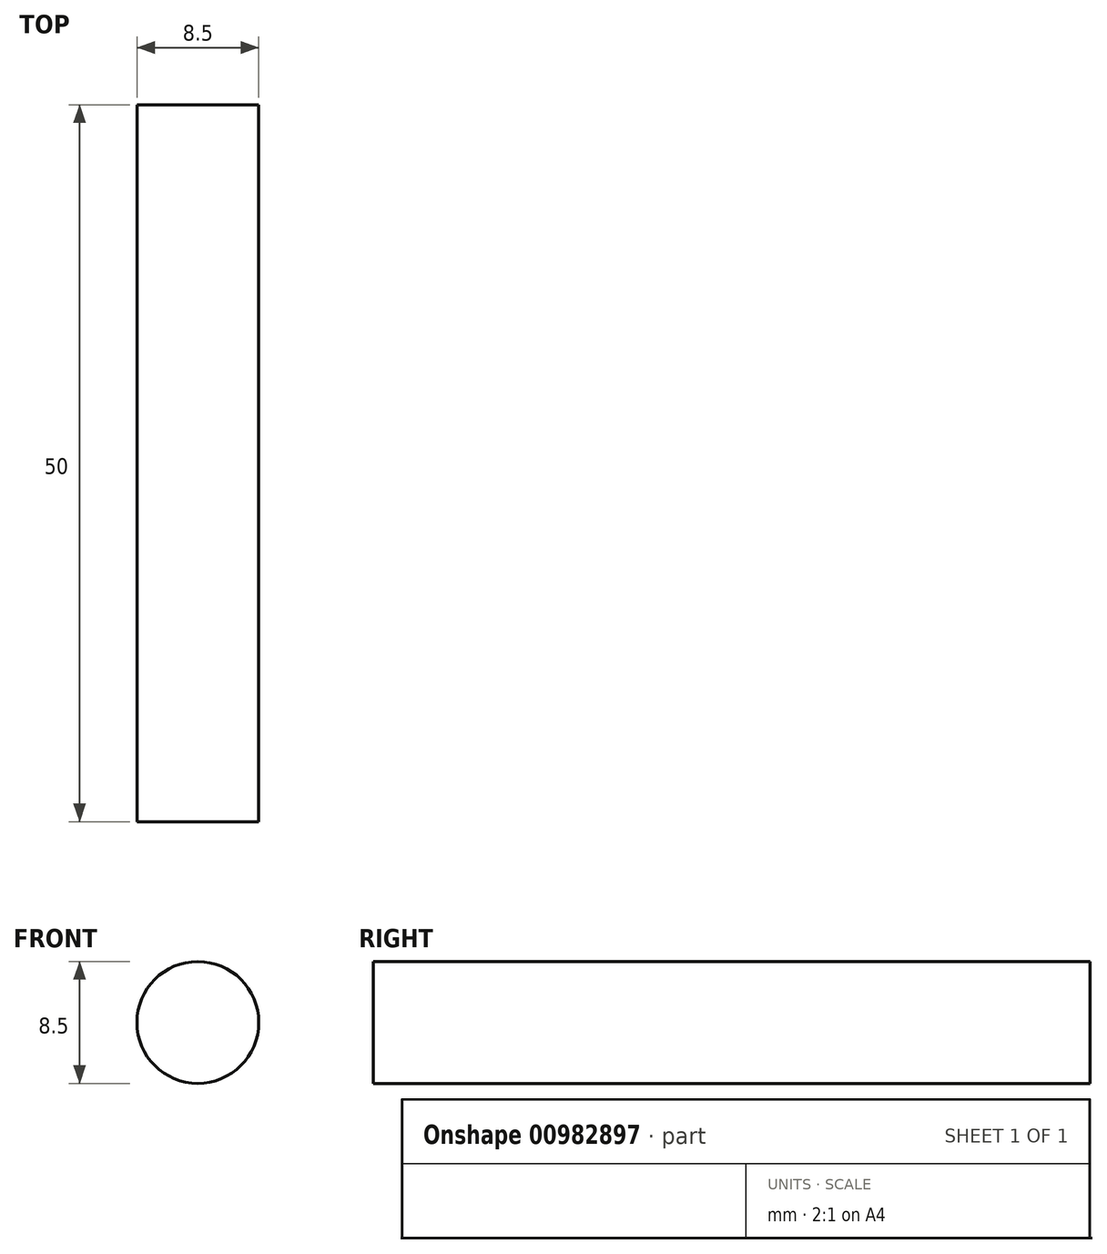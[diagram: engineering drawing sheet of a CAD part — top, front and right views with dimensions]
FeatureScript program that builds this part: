
annotation { "Feature Type Name" : "Feature", "Feature Type Description" : "" }
export const myFeature = defineFeature(function(context is Context, id is Id, definition is map)
    precondition{}
    {
        {
            var Q0;
            Q0=qCreatedBy(makeId("Top.planeOp"),FACE);
            var sketch = newSketch(context, id + "F0", { "sketchPlane" : qUnion([Q0])});
            skPoint(sketch, "E0", {"position": v(34.15, 0) * mm});
            skLineSegment(sketch, "E1", {"start": v(34.15, 25) * mm, "end": v(34.15, -25) * mm});
            skLineSegment(sketch, "E2", {"start": v(34.15, -25) * mm, "end": v(-34.15, -25) * mm});
            skLineSegment(sketch, "E3", {"start": v(-34.15, -25) * mm, "end": v(-34.15, 25) * mm});
            skLineSegment(sketch, "E4", {"start": v(-34.15, 25) * mm, "end": v(34.15, 25) * mm});
            skCircle(sketch, "E5", {"center": v(0, 0) * mm, "radius": 11 * mm});
            skLineSegment(sketch, "E6.bottom", {"start": v(15.5, -15.5) * mm, "end": v(-15.5, -15.5) * mm, "construction": true});
            skLineSegment(sketch, "E6.top", {"start": v(15.5, 15.5) * mm, "end": v(-15.5, 15.5) * mm, "construction": true});
            skLineSegment(sketch, "E6.left", {"start": v(15.5, -15.5) * mm, "end": v(15.5, 15.5) * mm, "construction": true});
            skLineSegment(sketch, "E6.right", {"start": v(-15.5, -15.5) * mm, "end": v(-15.5, 15.5) * mm, "construction": true});
            skCircle(sketch, "E7", {"center": v(-15.5, 15.5) * mm, "radius": 2 * mm});
            skCircle(sketch, "E8.1.0", {"center": v(-15.5, -15.5) * mm, "radius": 2 * mm});
            skCircle(sketch, "E8.2.0", {"center": v(15.5, -15.5) * mm, "radius": 2 * mm});
            skCircle(sketch, "E8.3.0", {"center": v(15.5, 15.5) * mm, "radius": 2 * mm});
            skSolve(sketch);
        }
        {
            var Q0;
            Q0=makeQuery(id+"F0.imprint","IMPRINT",FACE,{"disambiguationData":[TD([[makeQuery(id+"F0.imprint","IMPRINT",EDGE,{"derivedFrom":sQuery(id+"F0.wireOp",EDGE,"E1")}),-1.0]])]});
            extrude(context, id + "F1", {"entities" : qUnion([Q0]), "depth" : 15 * mm, "offsetDistance" : 25 * mm});
        }
        {
            var Q0;
            Q0=makeQuery(id+"F1.opExtrude","SWEPT_FACE",FACE,{"disambiguationData":[OSD([sQuery(id+"F0.wireOp",EDGE,"E2")])]});
            var sketch = newSketch(context, id + "F2", { "sketchPlane" : qUnion([Q0])});
            skCircle(sketch, "E9", {"center": v(-26.15, 7.5) * mm, "radius": 4.25 * mm});
            skPoint(sketch, "E9.centerSnap0", {"position": v(-34.15, 7.5) * mm});
            skCircle(sketch, "E10.MirrorC", {"center": v(26.15, 7.5) * mm, "radius": 4.25 * mm});
            skSolve(sketch);
        }
        {
            var Q0;
            Q0=makeQuery(id+"F2.imprint","IMPRINT",FACE,{"disambiguationData":[TD([[makeQuery(id+"F2.imprint","IMPRINT",EDGE,{"derivedFrom":sQuery(id+"F2.wireOp",EDGE,"E9")}),1.0]])]});
            var Q1;
            Q1=makeQuery(id+"F2.imprint","IMPRINT",FACE,{"disambiguationData":[TD([[makeQuery(id+"F2.imprint","IMPRINT",EDGE,{"derivedFrom":sQuery(id+"F2.wireOp",EDGE,"E10.MirrorC")}),-1.0]])]});
            extrude(context, id + "F3", {"entities" : qUnion([Q0, Q1]), "operationType" : NewBodyOperationType.REMOVE, "endBound" : BoundingType.UP_TO_NEXT, "oppositeDirection" : true, "depth" : 25 * mm, "offsetDistance" : 25 * mm});
        }
    });
